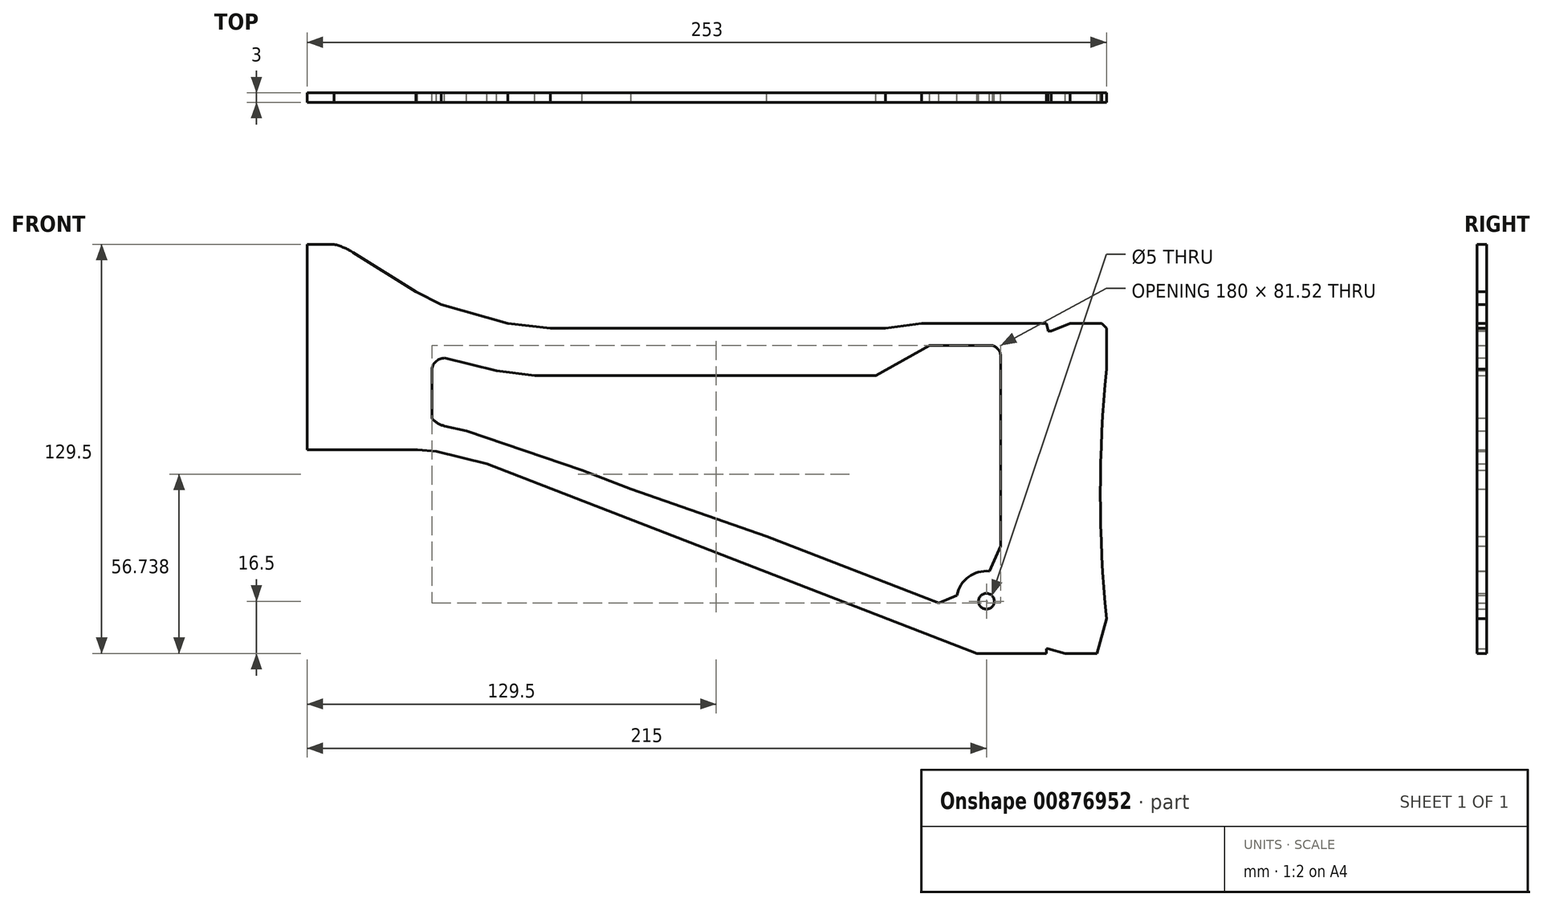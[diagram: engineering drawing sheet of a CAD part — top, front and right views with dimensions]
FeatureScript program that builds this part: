
annotation { "Feature Type Name" : "Feature", "Feature Type Description" : "" }
export const myFeature = defineFeature(function(context is Context, id is Id, definition is map)
    precondition{}
    {
        {
            var Q0;
            Q0=qCreatedBy(makeId("Front.planeOp"),FACE);
            var sketch = newSketch(context, id + "F0", { "sketchPlane" : qUnion([Q0])});
            skLineSegment(sketch, "E0", {"start": v(0, 0) * mm, "end": v(8.5, 0) * mm});
            skLineSegment(sketch, "E1", {"start": v(14.5, -2.5) * mm, "end": v(34.5, -15) * mm});
            skLineSegment(sketch, "E2", {"start": v(34.5, -15) * mm, "end": v(42.5, -19) * mm});
            skLineSegment(sketch, "E3", {"start": v(42.5, -19) * mm, "end": v(63.5, -25) * mm});
            skLineSegment(sketch, "E4", {"start": v(63.5, -25) * mm, "end": v(77, -26.5) * mm});
            skLineSegment(sketch, "E5", {"start": v(77, -26.5) * mm, "end": v(183, -26.5) * mm});
            skLineSegment(sketch, "E6", {"start": v(183, -26.5) * mm, "end": v(194.5, -25) * mm});
            skLineSegment(sketch, "E7", {"start": v(194.5, -25) * mm, "end": v(234, -25) * mm});
            skLineSegment(sketch, "E8", {"start": v(234, -25) * mm, "end": v(234.5, -27) * mm});
            skLineSegment(sketch, "E9", {"start": v(234.5, -27) * mm, "end": v(234.5, -27.5) * mm});
            skLineSegment(sketch, "E10", {"start": v(234.5, -27.5) * mm, "end": v(235.5, -27.5) * mm});
            skLineSegment(sketch, "E11", {"start": v(235.5, -27.5) * mm, "end": v(241.5, -25) * mm});
            skLineSegment(sketch, "E12", {"start": v(241.5, -25) * mm, "end": v(251.5, -25) * mm});
            skLineSegment(sketch, "E13", {"start": v(251.5, -25) * mm, "end": v(253, -26.5) * mm});
            skLineSegment(sketch, "E14", {"start": v(253, -26.5) * mm, "end": v(253, -39.5) * mm});
            skLineSegment(sketch, "E15", {"start": v(253, -118.5) * mm, "end": v(250, -129.5) * mm});
            skLineSegment(sketch, "E16", {"start": v(250, -129.5) * mm, "end": v(240, -129.5) * mm});
            skLineSegment(sketch, "E17", {"start": v(240, -129.5) * mm, "end": v(234.5, -128) * mm});
            skLineSegment(sketch, "E18", {"start": v(234.5, -128) * mm, "end": v(234, -128) * mm});
            skLineSegment(sketch, "E19", {"start": v(234, -128) * mm, "end": v(234, -129.5) * mm});
            skLineSegment(sketch, "E20", {"start": v(234, -129.5) * mm, "end": v(212, -129.5) * mm});
            skLineSegment(sketch, "E21", {"start": v(212, -129.5) * mm, "end": v(57, -69.5) * mm});
            skLineSegment(sketch, "E22", {"start": v(57, -69.5) * mm, "end": v(41, -65.5) * mm});
            skLineSegment(sketch, "E23", {"start": v(41, -65.5) * mm, "end": v(35, -65) * mm});
            skLineSegment(sketch, "E24", {"start": v(35, -65) * mm, "end": v(0, -65) * mm});
            skLineSegment(sketch, "E25", {"start": v(0, -65) * mm, "end": v(0, 0) * mm});
            skLineSegment(sketch, "E26", {"start": v(87, -41.5) * mm, "end": v(113, -41.5) * mm});
            skLineSegment(sketch, "E27", {"start": v(87, -71.5) * mm, "end": v(102.5, -77.5) * mm});
            skLineSegment(sketch, "E28", {"start": v(138, -41.5) * mm, "end": v(180, -41.5) * mm});
            skLineSegment(sketch, "E29", {"start": v(180, -41.5) * mm, "end": v(197, -32) * mm});
            skLineSegment(sketch, "E30", {"start": v(219.5, -35.5) * mm, "end": v(219.5, -95.5) * mm});
            skLineSegment(sketch, "E31", {"start": v(219.5, -95.5) * mm, "end": v(216, -103.5) * mm});
            skLineSegment(sketch, "E32", {"start": v(145.5, -92.43) * mm, "end": v(200, -113.52) * mm});
            skLineSegment(sketch, "E33", {"start": v(200, -113.52) * mm, "end": v(205.64, -111.11) * mm});
            skPoint(sketch, "E34", {"position": v(77, -41.5) * mm});
            skPoint(sketch, "E35", {"position": v(215, -113) * mm});
            skArc(sketch, "E36", {"start": v(216, -103.5) * mm, "mid": v(209.35, -105.3) * mm, "end": v(205.64, -111.11) * mm});
            skCircle(sketch, "E37", {"center": v(215, -113) * mm, "radius": 2.5 * mm});
            skArc(sketch, "E38", {"start": v(14.5, -2.5) * mm, "mid": v(11.6, -1) * mm, "end": v(8.5, 0) * mm});
            skArc(sketch, "E39", {"start": v(253, -39.5) * mm, "mid": v(251.05, -79) * mm, "end": v(253, -118.5) * mm});
            skPoint(sketch, "E40", {"position": v(253, -79) * mm});
            skLineSegment(sketch, "E41", {"start": v(217, -32) * mm, "end": v(197, -32) * mm});
            skLineSegment(sketch, "E42", {"start": v(102.5, -77.5) * mm, "end": v(145.5, -92.43) * mm});
            skLineSegment(sketch, "E43", {"start": v(113, -41.5) * mm, "end": v(138, -41.5) * mm});
            skLineSegment(sketch, "E44", {"start": v(77, -41.5) * mm, "end": v(87, -41.5) * mm});
            skLineSegment(sketch, "E45", {"start": v(87, -71.5) * mm, "end": v(50.5, -59) * mm});
            skLineSegment(sketch, "E46", {"start": v(50.5, -59) * mm, "end": v(43.5, -57.5) * mm});
            skLineSegment(sketch, "E47", {"start": v(39.5, -55) * mm, "end": v(39.5, -40) * mm});
            skLineSegment(sketch, "E48", {"start": v(43.5, -36) * mm, "end": v(60, -40) * mm});
            skLineSegment(sketch, "E49", {"start": v(60, -40) * mm, "end": v(72, -41.5) * mm});
            skLineSegment(sketch, "E50", {"start": v(72, -41.5) * mm, "end": v(77, -41.5) * mm});
            skArc(sketch, "E51", {"start": v(43.5, -57.5) * mm, "mid": v(41.28, -56.6) * mm, "end": v(39.5, -55) * mm});
            skArc(sketch, "E52", {"start": v(39.5, -40) * mm, "mid": v(40.67, -37.17) * mm, "end": v(43.5, -36) * mm});
            skArc(sketch, "E53", {"start": v(219.5, -35.5) * mm, "mid": v(218.81, -33.35) * mm, "end": v(217, -32) * mm});
            skSolve(sketch);
        }
        {
            var Q0;
            Q0=makeQuery(id+"F0.imprint","IMPRINT",FACE,{"disambiguationData":[TD([[makeQuery(id+"F0.imprint","IMPRINT",EDGE,{"derivedFrom":sQuery(id+"F0.wireOp",EDGE,"E0")}),-1.0]])]});
            extrude(context, id + "F1", {"entities" : qUnion([Q0]), "depth" : 3 * mm, "offsetDistance" : 25 * mm});
        }
    });
